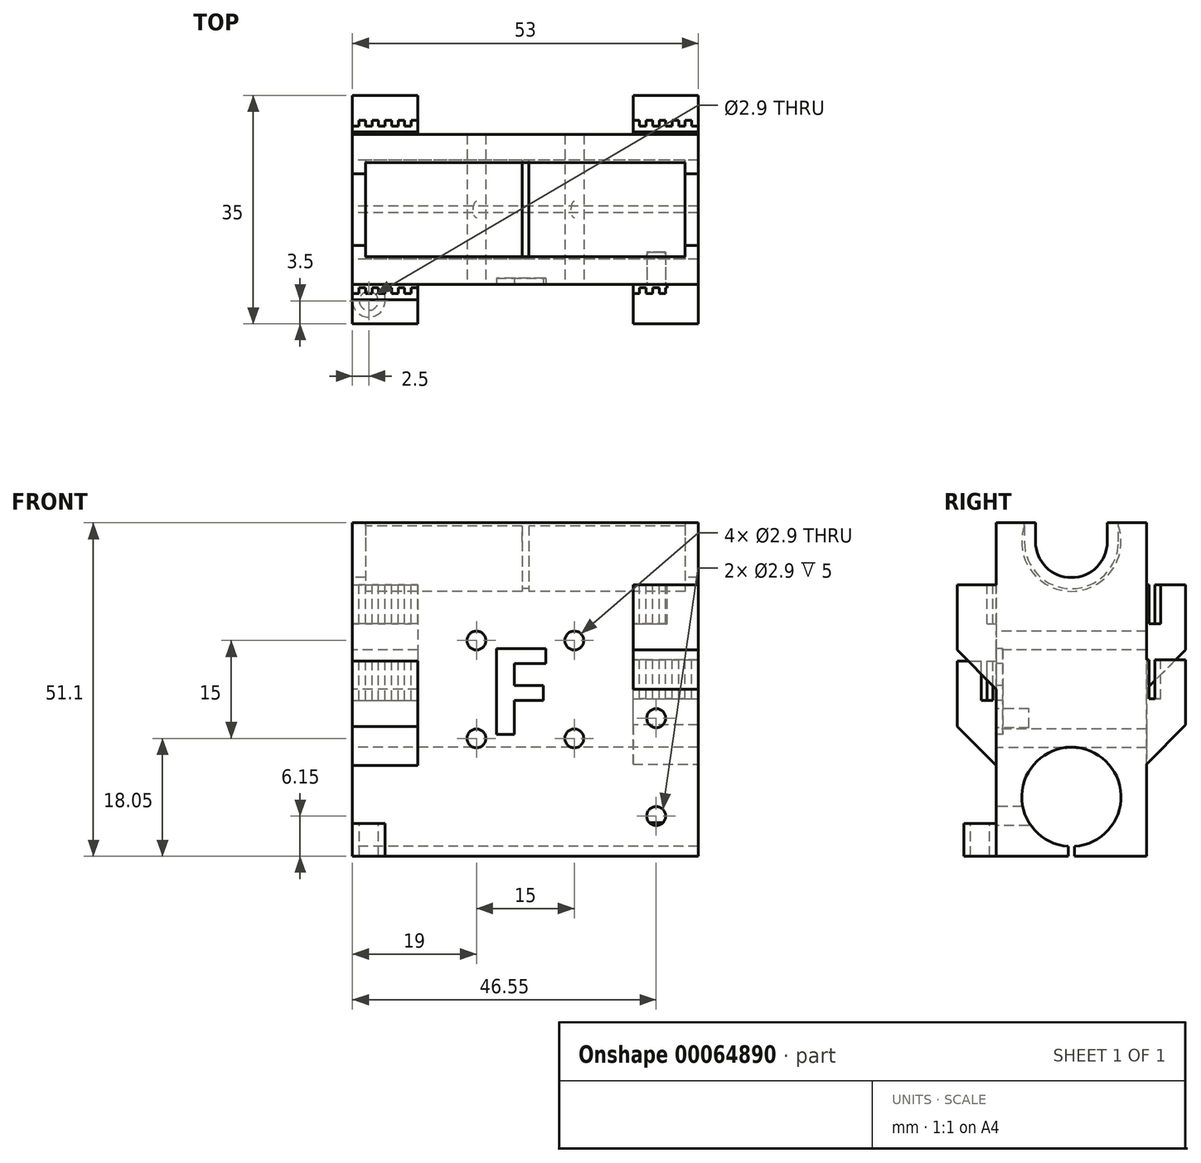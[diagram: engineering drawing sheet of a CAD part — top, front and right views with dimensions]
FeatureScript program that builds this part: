
annotation { "Feature Type Name" : "Feature", "Feature Type Description" : "" }
export const myFeature = defineFeature(function(context is Context, id is Id, definition is map)
    precondition{}
    {
        {
            assignVariable(context, id + "F0", {"name" : "LM_L", "anyValue" : 24});
        }
        {
            assignVariable(context, id + "F1", {"name" : "LM_D", "anyValue" : 15});
        }
        {
            assignVariable(context, id + "F2", {"name" : "InterAxe", "anyValue" : 39.1});
        }
        {
            var Q0;
            Q0=qCreatedBy(makeId("Top.planeOp"),FACE);
            var sketch = newSketch(context, id + "F3", { "sketchPlane" : qUnion([Q0])});
            skLineSegment(sketch, "E0.bottom", {"start": v(0, 0) * mm, "end": v(53, 0) * mm});
            skLineSegment(sketch, "E0.top", {"start": v(0, 23) * mm, "end": v(53, 23) * mm});
            skLineSegment(sketch, "E0.left", {"start": v(0, 0) * mm, "end": v(0, 23) * mm});
            skLineSegment(sketch, "E0.right", {"start": v(53, 0) * mm, "end": v(53, 23) * mm});
            skSolve(sketch);
        }
        {
            var Q0;
            Q0=qSketchRegion(id+"F3",true);
            extrude(context, id + "F4", {"entities" : qUnion([Q0]), "depth" : (getVariable(context, 'InterAxe') + getVariable(context, 'LM_D') + 1.5 - getVariable(context, 'LM_D') / 2 * 0.6) * mm});
        }
        {
            var Q0;
            Q0=makeQuery(id+"F4.opExtrude","SWEPT_FACE",FACE,{"disambiguationData":[OSD([sQuery(id+"F3.wireOp",EDGE,"E0.left")])]});
            var sketch = newSketch(context, id + "F5", { "sketchPlane" : qUnion([Q0])});
            skCircle(sketch, "E1", {"center": v(-11.5, 9.1) * mm, "radius": 7.6 * mm});
            skCircle(sketch, "E2", {"center": v(-11.5, 48.2) * mm, "radius": 5.5 * mm});
            skLineSegment(sketch, "E3", {"start": v(-23, 48.2) * mm, "end": v(0, 48.2) * mm, "construction": true});
            skLineSegment(sketch, "E4", {"start": v(-17, 51.1) * mm, "end": v(-17, 48.2) * mm});
            skLineSegment(sketch, "E5", {"start": v(-6, 51.1) * mm, "end": v(-6, 48.2) * mm});
            skLineSegment(sketch, "E6", {"start": v(-23, 9.1) * mm, "end": v(0, 9.1) * mm, "construction": true});
            skLineSegment(sketch, "E7", {"start": v(-11.5, 9.1) * mm, "end": v(-11.5, 0) * mm, "construction": true});
            skLineSegment(sketch, "E8", {"start": v(-11.5, 0) * mm, "end": v(-12, 0) * mm});
            skLineSegment(sketch, "E9", {"start": v(-12, 0) * mm, "end": v(-12, 1.52) * mm});
            skLineSegment(sketch, "E10", {"start": v(-12, 1.52) * mm, "end": v(-11, 1.52) * mm});
            skLineSegment(sketch, "E11", {"start": v(-11, 1.52) * mm, "end": v(-11, 0) * mm});
            skLineSegment(sketch, "E12", {"start": v(-11, 0) * mm, "end": v(-11.5, 0) * mm});
            skLineSegment(sketch, "E13", {"start": v(-11.5, 15.6) * mm, "end": v(-11.5, 16.7) * mm});
            skLineSegment(sketch, "E14", {"start": v(-11.5, 15.6) * mm, "end": v(-7, 15.22) * mm});
            skLineSegment(sketch, "E15", {"start": v(-11.5, 15.6) * mm, "end": v(-16, 15.22) * mm});
            skCircle(sketch, "E16", {"center": v(-11.5, 48.2) * mm, "radius": 7.6 * mm});
            skLineSegment(sketch, "E17", {"start": v(-3.9, 48.2) * mm, "end": v(-3.9, 51.1) * mm});
            skLineSegment(sketch, "E18", {"start": v(-19.1, 48.2) * mm, "end": v(-19.1, 51.1) * mm});
            skLineSegment(sketch, "E19", {"start": v(-3.9, 51.1) * mm, "end": v(-4.3, 51.1) * mm});
            skLineSegment(sketch, "E20", {"start": v(-4.3, 51.1) * mm, "end": v(-4.3, 50.63) * mm});
            skLineSegment(sketch, "E21", {"start": v(-19.1, 51.1) * mm, "end": v(-18.7, 51.1) * mm});
            skLineSegment(sketch, "E22", {"start": v(-18.7, 51.1) * mm, "end": v(-18.7, 50.63) * mm});
            skCircle(sketch, "E23", {"center": v(-11.5, 48.2) * mm, "radius": 7.2 * mm});
            skLineSegment(sketch, "E24", {"start": v(-18.7, 50.63) * mm, "end": v(-18.7, 48.2) * mm});
            skLineSegment(sketch, "E25", {"start": v(-4.3, 50.63) * mm, "end": v(-4.3, 48.2) * mm});
            skSolve(sketch);
        }
        {
            var Q0;
            {var subQ0=sQuery(id+"F5.wireOp",EDGE,"E14");var subQ1=sQuery(id+"F5.wireOp",EDGE,"E1");var subQ3=makeQuery(id+"F5.imprint","INTERSECT",VERTEX,{"disambiguationData":[OD(0.0)],"derivedFrom":[subQ1,subQ0]});Q0=makeQuery(id+"F5.imprint","IMPRINT",FACE,{"disambiguationData":[TD([[makeQuery(id+"F5.imprint","IMPRINT",EDGE,{"disambiguationData":[TD([[subQ3,-1.0]])],"derivedFrom":subQ1}),1.0]])]});}
            var Q1;
            {var subQ0=sQuery(id+"F5.wireOp",EDGE,"E15");var subQ1=sQuery(id+"F5.wireOp",EDGE,"E1");var subQ3=makeQuery(id+"F5.imprint","INTERSECT",VERTEX,{"disambiguationData":[OD(0.0)],"derivedFrom":[subQ1,subQ0]});Q1=makeQuery(id+"F5.imprint","IMPRINT",FACE,{"disambiguationData":[TD([[makeQuery(id+"F5.imprint","IMPRINT",EDGE,{"disambiguationData":[TD([[subQ3,1.0]])],"derivedFrom":subQ1}),1.0]])]});}
            var Q2;
            Q2=makeQuery(id+"F5.imprint","IMPRINT",FACE,{"disambiguationData":[TD([[makeQuery(id+"F5.imprint","IMPRINT",EDGE,{"derivedFrom":sQuery(id+"F5.wireOp",EDGE,"E8")}),-1.0]])]});
            var Q3;
            {var subQ0=sQuery(id+"F5.wireOp",EDGE,"E10");Q3=makeQuery(id+"F5.imprint","IMPRINT",FACE,{"disambiguationData":[TD([[makeQuery(id+"F5.imprint","IMPRINT",EDGE,{"derivedFrom":subQ0}),-1.0]])]});}
            var Q4;
            {var subQ3=sQuery(id+"F5.wireOp",EDGE,"E13");Q4=makeQuery(id+"F5.imprint","IMPRINT",FACE,{"disambiguationData":[TD([[makeQuery(id+"F5.imprint","IMPRINT",EDGE,{"derivedFrom":subQ3}),-1.0]])]});}
            var Q5;
            {var subQ3=sQuery(id+"F5.wireOp",EDGE,"E13");Q5=makeQuery(id+"F5.imprint","IMPRINT",FACE,{"disambiguationData":[TD([[makeQuery(id+"F5.imprint","IMPRINT",EDGE,{"derivedFrom":subQ3}),1.0]])]});}
            var Q6;
            {var subQ7=sQuery(id+"F5.wireOp",EDGE,"E10");Q6=makeQuery(id+"F5.imprint","IMPRINT",FACE,{"disambiguationData":[TD([[makeQuery(id+"F5.imprint","IMPRINT",EDGE,{"derivedFrom":subQ7}),1.0]])]});}
            var Q7;
            {var subQ3=sQuery(id+"F5.wireOp",EDGE,"E5");Q7=makeQuery(id+"F5.imprint","IMPRINT",FACE,{"disambiguationData":[TD([[makeQuery(id+"F5.imprint","IMPRINT",EDGE,{"derivedFrom":subQ3}),-1.0]])]});}
            var Q8;
            {var subQ0=sQuery(id+"F5.wireOp",EDGE,"E4");Q8=makeQuery(id+"F5.imprint","IMPRINT",FACE,{"disambiguationData":[TD([[makeQuery(id+"F5.imprint","IMPRINT",EDGE,{"derivedFrom":subQ0}),1.0]])]});}
            var Q9;
            {var subQ0=sQuery(id+"F5.wireOp",EDGE,"E4");Q9=makeQuery(id+"F5.imprint","IMPRINT",FACE,{"disambiguationData":[TD([[makeQuery(id+"F5.imprint","IMPRINT",EDGE,{"derivedFrom":subQ0}),1.0]])]});}
            var Q10;
            {var subQ3=sQuery(id+"F5.wireOp",EDGE,"E5");Q10=makeQuery(id+"F5.imprint","IMPRINT",FACE,{"disambiguationData":[TD([[makeQuery(id+"F5.imprint","IMPRINT",EDGE,{"derivedFrom":subQ3}),-1.0]])]});}
            var Q11;
            {var subQ1=sQuery(id+"F5.wireOp",EDGE,"E2");var subQ4=makeQuery(id+"F5.imprint","INTERSECT",VERTEX,{"derivedFrom":[subQ1,sQuery(id+"F5.wireOp",EDGE,"E5")]});Q11=makeQuery(id+"F5.imprint","IMPRINT",FACE,{"disambiguationData":[TD([[makeQuery(id+"F5.imprint","IMPRINT",EDGE,{"disambiguationData":[TD([[subQ4,-1.0]])],"derivedFrom":subQ1}),1.0]])]});}
            extrude(context, id + "F6", {"entities" : qUnion([Q0, Q1, Q2, Q3, Q4, Q5, Q6, Q7, Q8, Q9, Q10, Q11]), "operationType" : NewBodyOperationType.REMOVE, "endBound" : BoundingType.THROUGH_ALL, "oppositeDirection" : true, "depth" : 25 * mm});
        }
        {
            var Q0;
            {var subQ3=sQuery(id+"F5.wireOp",EDGE,"E4");Q0=makeQuery(id+"F5.imprint","IMPRINT",FACE,{"disambiguationData":[TD([[makeQuery(id+"F5.imprint","IMPRINT",EDGE,{"derivedFrom":subQ3}),-1.0]])]});}
            var Q1;
            {var subQ9=sQuery(id+"F5.wireOp",EDGE,"Eceb68xk-Og1x-mNxy-NVvu-haE7G9XDnVFp");Q1=makeQuery(id+"F5.imprint","IMPRINT",FACE,{"disambiguationData":[TD([[makeQuery(id+"F5.imprint","IMPRINT",EDGE,{"derivedFrom":subQ9}),-1.0]])]});}
            var Q2;
            {var subQ2=sQuery(id+"F5.wireOp",EDGE,"0G9KEAjU-obAv-1t8S-ChZ4-jWTQQU7pxxCP");Q2=makeQuery(id+"F5.imprint","IMPRINT",FACE,{"disambiguationData":[TD([[makeQuery(id+"F5.imprint","IMPRINT",EDGE,{"derivedFrom":subQ2}),-1.0]])]});}
            var Q3;
            {var subQ2=sQuery(id+"F5.wireOp",EDGE,"Eceb68xk-Og1x-mNxy-NVvu-haE7G9XDnVFp");Q3=makeQuery(id+"F5.imprint","IMPRINT",FACE,{"disambiguationData":[TD([[makeQuery(id+"F5.imprint","IMPRINT",EDGE,{"derivedFrom":subQ2}),1.0]])]});}
            var Q4;
            {var subQ0=sQuery(id+"F5.wireOp",EDGE,"E25");Q4=makeQuery(id+"F5.imprint","IMPRINT",FACE,{"disambiguationData":[TD([[makeQuery(id+"F5.imprint","IMPRINT",EDGE,{"derivedFrom":subQ0}),-1.0]])]});}
            var Q5;
            {var subQ0=sQuery(id+"F5.wireOp",EDGE,"E24");Q5=makeQuery(id+"F5.imprint","IMPRINT",FACE,{"disambiguationData":[TD([[makeQuery(id+"F5.imprint","IMPRINT",EDGE,{"derivedFrom":subQ0}),1.0]])]});}
            var Q6;
            {var subQ0=sQuery(id+"F5.wireOp",EDGE,"E22");Q6=makeQuery(id+"F5.imprint","IMPRINT",FACE,{"disambiguationData":[TD([[makeQuery(id+"F5.imprint","IMPRINT",EDGE,{"derivedFrom":subQ0}),1.0]])]});}
            var Q7;
            {var subQ0=sQuery(id+"F5.wireOp",EDGE,"E24");Q7=makeQuery(id+"F5.imprint","IMPRINT",FACE,{"disambiguationData":[TD([[makeQuery(id+"F5.imprint","IMPRINT",EDGE,{"derivedFrom":subQ0}),-1.0]])]});}
            var Q8;
            {var subQ0=sQuery(id+"F5.wireOp",EDGE,"E20");Q8=makeQuery(id+"F5.imprint","IMPRINT",FACE,{"disambiguationData":[TD([[makeQuery(id+"F5.imprint","IMPRINT",EDGE,{"derivedFrom":subQ0}),-1.0]])]});}
            extrude(context, id + "F7", {"entities" : qUnion([Q0, Q1, Q2, Q3, Q4, Q5, Q6, Q7, Q8]), "operationType" : NewBodyOperationType.REMOVE, "oppositeDirection" : true, "depth" : (3 + getVariable(context, 'LM_L') * 2) * mm});
        }
        {
            var Q0;
            {var subQ0=sQuery(id+"F5.wireOp",EDGE,"E24");Q0=makeQuery(id+"F5.imprint","IMPRINT",FACE,{"disambiguationData":[TD([[makeQuery(id+"F5.imprint","IMPRINT",EDGE,{"derivedFrom":subQ0}),-1.0]])]});}
            extrude(context, id + "F8", {"entities" : qUnion([Q0]), "operationType" : NewBodyOperationType.ADD, "oppositeDirection" : true, "depth" : (3 + getVariable(context, 'LM_L')) * mm});
        }
        {
            var Q0;
            {var subQ3=sQuery(id+"F5.wireOp",EDGE,"E4");Q0=makeQuery(id+"F5.imprint","IMPRINT",FACE,{"disambiguationData":[TD([[makeQuery(id+"F5.imprint","IMPRINT",EDGE,{"derivedFrom":subQ3}),-1.0]])]});}
            var Q1;
            {var subQ0=sQuery(id+"F5.wireOp",EDGE,"E20");Q1=makeQuery(id+"F5.imprint","IMPRINT",FACE,{"disambiguationData":[TD([[makeQuery(id+"F5.imprint","IMPRINT",EDGE,{"derivedFrom":subQ0}),-1.0]])]});}
            var Q2;
            {var subQ0=sQuery(id+"F5.wireOp",EDGE,"E22");Q2=makeQuery(id+"F5.imprint","IMPRINT",FACE,{"disambiguationData":[TD([[makeQuery(id+"F5.imprint","IMPRINT",EDGE,{"derivedFrom":subQ0}),1.0]])]});}
            var Q3;
            {var subQ0=sQuery(id+"F5.wireOp",EDGE,"E24");Q3=makeQuery(id+"F5.imprint","IMPRINT",FACE,{"disambiguationData":[TD([[makeQuery(id+"F5.imprint","IMPRINT",EDGE,{"derivedFrom":subQ0}),-1.0]])]});}
            var Q4;
            {var subQ0=sQuery(id+"F5.wireOp",EDGE,"E24");Q4=makeQuery(id+"F5.imprint","IMPRINT",FACE,{"disambiguationData":[TD([[makeQuery(id+"F5.imprint","IMPRINT",EDGE,{"derivedFrom":subQ0}),1.0]])]});}
            var Q5;
            {var subQ0=sQuery(id+"F5.wireOp",EDGE,"E4");Q5=makeQuery(id+"F5.imprint","IMPRINT",FACE,{"disambiguationData":[TD([[makeQuery(id+"F5.imprint","IMPRINT",EDGE,{"derivedFrom":subQ0}),1.0]])]});}
            var Q6;
            {var subQ0=sQuery(id+"F5.wireOp",EDGE,"E25");Q6=makeQuery(id+"F5.imprint","IMPRINT",FACE,{"disambiguationData":[TD([[makeQuery(id+"F5.imprint","IMPRINT",EDGE,{"derivedFrom":subQ0}),-1.0]])]});}
            extrude(context, id + "F9", {"entities" : qUnion([Q0, Q1, Q2, Q3, Q4, Q5, Q6]), "operationType" : NewBodyOperationType.REMOVE, "oppositeDirection" : true, "depth" : (2 + getVariable(context, 'LM_L')) * mm});
        }
        {
            var Q0;
            {var subQ3=sQuery(id+"F5.wireOp",EDGE,"E4");Q0=makeQuery(id+"F5.imprint","IMPRINT",FACE,{"disambiguationData":[TD([[makeQuery(id+"F5.imprint","IMPRINT",EDGE,{"derivedFrom":subQ3}),-1.0]])]});}
            var Q1;
            {var subQ3=sQuery(id+"F5.wireOp",EDGE,"E18");Q1=makeQuery(id+"F5.imprint","IMPRINT",FACE,{"disambiguationData":[TD([[makeQuery(id+"F5.imprint","IMPRINT",EDGE,{"derivedFrom":subQ3}),-1.0]])]});}
            var Q2;
            {var subQ3=sQuery(id+"F5.wireOp",EDGE,"E17");Q2=makeQuery(id+"F5.imprint","IMPRINT",FACE,{"disambiguationData":[TD([[makeQuery(id+"F5.imprint","IMPRINT",EDGE,{"derivedFrom":subQ3}),1.0]])]});}
            var Q3;
            {var subQ0=sQuery(id+"F5.wireOp",EDGE,"E24");Q3=makeQuery(id+"F5.imprint","IMPRINT",FACE,{"disambiguationData":[TD([[makeQuery(id+"F5.imprint","IMPRINT",EDGE,{"derivedFrom":subQ0}),-1.0]])]});}
            var Q4;
            {var subQ0=sQuery(id+"F5.wireOp",EDGE,"E24");Q4=makeQuery(id+"F5.imprint","IMPRINT",FACE,{"disambiguationData":[TD([[makeQuery(id+"F5.imprint","IMPRINT",EDGE,{"derivedFrom":subQ0}),1.0]])]});}
            var Q5;
            {var subQ0=sQuery(id+"F5.wireOp",EDGE,"E22");Q5=makeQuery(id+"F5.imprint","IMPRINT",FACE,{"disambiguationData":[TD([[makeQuery(id+"F5.imprint","IMPRINT",EDGE,{"derivedFrom":subQ0}),1.0]])]});}
            var Q6;
            {var subQ0=sQuery(id+"F5.wireOp",EDGE,"E25");Q6=makeQuery(id+"F5.imprint","IMPRINT",FACE,{"disambiguationData":[TD([[makeQuery(id+"F5.imprint","IMPRINT",EDGE,{"derivedFrom":subQ0}),-1.0]])]});}
            var Q7;
            {var subQ0=sQuery(id+"F5.wireOp",EDGE,"E20");Q7=makeQuery(id+"F5.imprint","IMPRINT",FACE,{"disambiguationData":[TD([[makeQuery(id+"F5.imprint","IMPRINT",EDGE,{"derivedFrom":subQ0}),-1.0]])]});}
            extrude(context, id + "F10", {"entities" : qUnion([Q0, Q1, Q2, Q3, Q4, Q5, Q6, Q7]), "operationType" : NewBodyOperationType.ADD, "oppositeDirection" : true, "depth" : 2 * mm});
        }
        {
            var Q0;
            Q0=makeQuery(id+"F4.opExtrude","SWEPT_FACE",FACE,{"disambiguationData":[OSD([sQuery(id+"F3.wireOp",EDGE,"E0.bottom")])]});
            var sketch = newSketch(context, id + "F11", { "sketchPlane" : qUnion([Q0])});
            skLineSegment(sketch, "E26.bottom", {"start": v(0, 29.9) * mm, "end": v(10, 29.9) * mm});
            skLineSegment(sketch, "E26.top", {"start": v(0, 9.9) * mm, "end": v(10, 9.9) * mm});
            skLineSegment(sketch, "E26.left", {"start": v(0, 29.9) * mm, "end": v(0, 9.9) * mm});
            skLineSegment(sketch, "E26.right", {"start": v(10, 29.9) * mm, "end": v(10, 9.9) * mm});
            skLineSegment(sketch, "E27.bottom", {"start": v(53, 41.6) * mm, "end": v(43, 41.6) * mm});
            skLineSegment(sketch, "E27.top", {"start": v(53, 21.6) * mm, "end": v(43, 21.6) * mm});
            skLineSegment(sketch, "E27.left", {"start": v(53, 41.6) * mm, "end": v(53, 21.6) * mm});
            skLineSegment(sketch, "E27.right", {"start": v(43, 41.6) * mm, "end": v(43, 21.6) * mm});
            skPoint(sketch, "E28", {"position": v(0, 48.1) * mm});
            skPoint(sketch, "E29", {"position": v(0, 9.4) * mm});
            skSolve(sketch);
        }
        {
            var Q0;
            Q0=qSketchRegion(id+"F11",true);
            extrude(context, id + "F12", {"entities" : qUnion([Q0]), "operationType" : NewBodyOperationType.ADD, "depth" : 6 * mm});
        }
        {
            var Q0;
            Q0=makeQuery(id+"F12.opExtrude","CAP_EDGE",EDGE,{"disambiguationData":[OSD([sQuery(id+"F11.wireOp",EDGE,"E26.top")])],"isStart":false});
            var Q1;
            Q1=makeQuery(id+"F12.opExtrude","CAP_EDGE",EDGE,{"disambiguationData":[OSD([sQuery(id+"F11.wireOp",EDGE,"E27.top")])],"isStart":false});
            chamfer(context, id + "F13", {"entities" : qUnion([Q0, Q1]), "width" : 10 * mm, "tangentPropagation" : true});
        }
        {
            var Q0;
            Q0=makeQuery(id+"F12.opExtrude","SWEPT_FACE",FACE,{"disambiguationData":[OSD([sQuery(id+"F11.wireOp",EDGE,"E26.bottom")])]});
            var sketch = newSketch(context, id + "F14", { "sketchPlane" : qUnion([Q0])});
            skLineSegment(sketch, "E30.left", {"start": v(0, -2.3) * mm, "end": v(0, -0.5) * mm});
            skLineSegment(sketch, "E31", {"start": v(6, -1.4) * mm, "end": v(7, -1.4) * mm});
            skLineSegment(sketch, "E32", {"start": v(4, -1.4) * mm, "end": v(5, -1.4) * mm});
            skLineSegment(sketch, "E33", {"start": v(0, -1.4) * mm, "end": v(1, -1.4) * mm});
            skLineSegment(sketch, "E34", {"start": v(7, -0.5) * mm, "end": v(8, -0.5) * mm});
            skLineSegment(sketch, "E35", {"start": v(2, -1.4) * mm, "end": v(3, -1.4) * mm});
            skLineSegment(sketch, "E36", {"start": v(3, -0.5) * mm, "end": v(4, -0.5) * mm});
            skLineSegment(sketch, "E37", {"start": v(8, -1.4) * mm, "end": v(9, -1.4) * mm});
            skLineSegment(sketch, "E38", {"start": v(8, -0.5) * mm, "end": v(8, -1.4) * mm});
            skLineSegment(sketch, "E39", {"start": v(9, -1.4) * mm, "end": v(9, -0.5) * mm});
            skLineSegment(sketch, "E40", {"start": v(10, -0.5) * mm, "end": v(10, -1.4) * mm});
            skLineSegment(sketch, "E41", {"start": v(6, -0.5) * mm, "end": v(6, -1.4) * mm});
            skLineSegment(sketch, "E42", {"start": v(2, -0.5) * mm, "end": v(2, -1.4) * mm});
            skLineSegment(sketch, "E43", {"start": v(1, -0.5) * mm, "end": v(2, -0.5) * mm});
            skLineSegment(sketch, "E44", {"start": v(1, -1.4) * mm, "end": v(1, -0.5) * mm});
            skLineSegment(sketch, "E45", {"start": v(9, -0.5) * mm, "end": v(10, -0.5) * mm});
            skLineSegment(sketch, "E46", {"start": v(5, -0.5) * mm, "end": v(6, -0.5) * mm});
            skLineSegment(sketch, "E47", {"start": v(5, -1.4) * mm, "end": v(5, -0.5) * mm});
            skLineSegment(sketch, "E48", {"start": v(3, -1.4) * mm, "end": v(3, -0.5) * mm});
            skLineSegment(sketch, "E49", {"start": v(4, -0.5) * mm, "end": v(4, -1.4) * mm});
            skLineSegment(sketch, "E50", {"start": v(7, -1.4) * mm, "end": v(7, -0.5) * mm});
            skLineSegment(sketch, "E51", {"start": v(0, -0.5) * mm, "end": v(0, -1.4) * mm});
            skLineSegment(sketch, "E52", {"start": v(10, -1.4) * mm, "end": v(10, -2.3) * mm});
            skLineSegment(sketch, "E53", {"start": v(0, -2.3) * mm, "end": v(10, -2.3) * mm});
            skLineSegment(sketch, "E54", {"start": v(5.3, -0.5) * mm, "end": v(5.3, 0) * mm});
            skSolve(sketch);
        }
        {
            var Q0;
            Q0=qSketchRegion(id+"F14",true);
            extrude(context, id + "F15", {"entities" : qUnion([Q0]), "operationType" : NewBodyOperationType.REMOVE, "oppositeDirection" : true, "depth" : 6 * mm});
        }
        {
            var Q0;
            Q0=makeQuery(id+"F12.opExtrude","SWEPT_FACE",FACE,{"disambiguationData":[OSD([sQuery(id+"F11.wireOp",EDGE,"E27.bottom")])]});
            var sketch = newSketch(context, id + "F16", { "sketchPlane" : qUnion([Q0])});
            skLineSegment(sketch, "E55.left", {"start": v(43, -2.3) * mm, "end": v(43, -0.5) * mm});
            skLineSegment(sketch, "E56", {"start": v(49, -1.4) * mm, "end": v(50, -1.4) * mm});
            skLineSegment(sketch, "E57", {"start": v(47, -1.4) * mm, "end": v(48, -1.4) * mm});
            skLineSegment(sketch, "E58", {"start": v(43, -1.4) * mm, "end": v(44, -1.4) * mm});
            skLineSegment(sketch, "E59", {"start": v(50, -0.5) * mm, "end": v(51, -0.5) * mm});
            skLineSegment(sketch, "E60", {"start": v(45, -1.4) * mm, "end": v(46, -1.4) * mm});
            skLineSegment(sketch, "E61", {"start": v(46, -0.5) * mm, "end": v(47, -0.5) * mm});
            skLineSegment(sketch, "E62", {"start": v(51, -1.4) * mm, "end": v(52, -1.4) * mm});
            skLineSegment(sketch, "E63", {"start": v(51, -0.5) * mm, "end": v(51, -1.4) * mm});
            skLineSegment(sketch, "E64", {"start": v(52, -1.4) * mm, "end": v(52, -0.5) * mm});
            skLineSegment(sketch, "E65", {"start": v(53, -0.5) * mm, "end": v(53, -1.4) * mm});
            skLineSegment(sketch, "E66", {"start": v(49, -0.5) * mm, "end": v(49, -1.4) * mm});
            skLineSegment(sketch, "E67", {"start": v(45, -0.5) * mm, "end": v(45, -1.4) * mm});
            skLineSegment(sketch, "E68", {"start": v(44, -0.5) * mm, "end": v(45, -0.5) * mm});
            skLineSegment(sketch, "E69", {"start": v(44, -1.4) * mm, "end": v(44, -0.5) * mm});
            skLineSegment(sketch, "E70", {"start": v(52, -0.5) * mm, "end": v(53, -0.5) * mm});
            skLineSegment(sketch, "E71", {"start": v(48, -0.5) * mm, "end": v(49, -0.5) * mm});
            skLineSegment(sketch, "E72", {"start": v(48, -1.4) * mm, "end": v(48, -0.5) * mm});
            skLineSegment(sketch, "E73", {"start": v(46, -1.4) * mm, "end": v(46, -0.5) * mm});
            skLineSegment(sketch, "E74", {"start": v(47, -0.5) * mm, "end": v(47, -1.4) * mm});
            skLineSegment(sketch, "E75", {"start": v(50, -1.4) * mm, "end": v(50, -0.5) * mm});
            skLineSegment(sketch, "E76", {"start": v(43, -0.5) * mm, "end": v(43, -1.4) * mm});
            skLineSegment(sketch, "E77", {"start": v(53, -1.4) * mm, "end": v(53, -2.3) * mm});
            skLineSegment(sketch, "E78", {"start": v(43, -2.3) * mm, "end": v(53, -2.3) * mm});
            skLineSegment(sketch, "E79", {"start": v(48.23, -0.5) * mm, "end": v(48.23, 0) * mm});
            skSolve(sketch);
        }
        {
            var Q0;
            Q0=makeQuery(id+"F4.opExtrude","SWEPT_FACE",FACE,{"disambiguationData":[OSD([sQuery(id+"F3.wireOp",EDGE,"E0.top")])]});
            var sketch = newSketch(context, id + "F17", { "sketchPlane" : qUnion([Q0])});
            skLineSegment(sketch, "E80.bottom", {"start": v(-53, 10.1) * mm, "end": v(-43, 10.1) * mm});
            skLineSegment(sketch, "E80.top", {"start": v(-53, 30.1) * mm, "end": v(-43, 30.1) * mm});
            skLineSegment(sketch, "E80.left", {"start": v(-53, 10.1) * mm, "end": v(-53, 30.1) * mm});
            skLineSegment(sketch, "E80.right", {"start": v(-43, 10.1) * mm, "end": v(-43, 30.1) * mm});
            skLineSegment(sketch, "E81.bottom", {"start": v(0, 41.6) * mm, "end": v(-10, 41.6) * mm});
            skLineSegment(sketch, "E81.top", {"start": v(0, 21.6) * mm, "end": v(-10, 21.6) * mm});
            skLineSegment(sketch, "E81.left", {"start": v(0, 41.6) * mm, "end": v(0, 21.6) * mm});
            skLineSegment(sketch, "E81.right", {"start": v(-10, 41.6) * mm, "end": v(-10, 21.6) * mm});
            skSolve(sketch);
        }
        {
            var Q0;
            Q0=qSketchRegion(id+"F17",true);
            extrude(context, id + "F18", {"entities" : qUnion([Q0]), "operationType" : NewBodyOperationType.ADD, "depth" : 6 * mm});
        }
        {
            var Q0;
            Q0=makeQuery(id+"F18.opExtrude","SWEPT_FACE",FACE,{"disambiguationData":[OSD([sQuery(id+"F17.wireOp",EDGE,"E80.top")])]});
            var sketch = newSketch(context, id + "F19", { "sketchPlane" : qUnion([Q0])});
            skLineSegment(sketch, "E82", {"start": v(45, 23.4) * mm, "end": v(46, 23.4) * mm});
            skLineSegment(sketch, "E83", {"start": v(46, 24.3) * mm, "end": v(47, 24.3) * mm});
            skLineSegment(sketch, "E84", {"start": v(52, 24.3) * mm, "end": v(53, 24.3) * mm});
            skLineSegment(sketch, "E85", {"start": v(53, 23.4) * mm, "end": v(53, 23.4) * mm});
            skLineSegment(sketch, "E86", {"start": v(43, 23.4) * mm, "end": v(53, 23.4) * mm});
            skLineSegment(sketch, "E87", {"start": v(48, 23.4) * mm, "end": v(48, 23) * mm});
            skLineSegment(sketch, "E88", {"start": v(43, 25.2) * mm, "end": v(53, 25.2) * mm});
            skLineSegment(sketch, "E89.bottom", {"start": v(47, 24.3) * mm, "end": v(46, 24.3) * mm});
            skLineSegment(sketch, "E89.top", {"start": v(47, 25.2) * mm, "end": v(46, 25.2) * mm});
            skLineSegment(sketch, "E90.top", {"start": v(48, 25.2) * mm, "end": v(49, 25.2) * mm});
            skLineSegment(sketch, "E91.top", {"start": v(44, 25.2) * mm, "end": v(45, 25.2) * mm});
            skLineSegment(sketch, "E92", {"start": v(53, 24.3) * mm, "end": v(43, 24.3) * mm, "construction": true});
            skLineSegment(sketch, "E93", {"start": v(52, 24.3) * mm, "end": v(52, 25.2) * mm});
            skLineSegment(sketch, "E94.1.0.0", {"start": v(51, 24.3) * mm, "end": v(51, 25.2) * mm});
            skLineSegment(sketch, "E94.2.0.0", {"start": v(50, 24.3) * mm, "end": v(50, 25.2) * mm});
            skLineSegment(sketch, "E94.3.0.0", {"start": v(49, 24.3) * mm, "end": v(49, 25.2) * mm});
            skLineSegment(sketch, "E94.4.0.0", {"start": v(48, 24.3) * mm, "end": v(48, 25.2) * mm});
            skLineSegment(sketch, "E94.5.0.0", {"start": v(47, 24.3) * mm, "end": v(47, 25.2) * mm});
            skLineSegment(sketch, "E94.6.0.0", {"start": v(46, 24.3) * mm, "end": v(46, 25.2) * mm});
            skLineSegment(sketch, "E94.7.0.0", {"start": v(45, 24.3) * mm, "end": v(45, 25.2) * mm});
            skLineSegment(sketch, "E94.8.0.0", {"start": v(44, 24.3) * mm, "end": v(44, 25.2) * mm});
            skLineSegment(sketch, "E94.direction1", {"start": v(52, 24.3) * mm, "end": v(51, 24.3) * mm, "construction": true});
            skLineSegment(sketch, "E95", {"start": v(51, 24.3) * mm, "end": v(50, 24.3) * mm});
            skLineSegment(sketch, "E96", {"start": v(49, 24.3) * mm, "end": v(48, 24.3) * mm});
            skLineSegment(sketch, "E97", {"start": v(45, 24.3) * mm, "end": v(44, 24.3) * mm});
            skSolve(sketch);
        }
        {
            var Q0;
            {var subQ10=sQuery(id+"F19.wireOp",EDGE,"E84");Q0=makeQuery(id+"F19.imprint","IMPRINT",FACE,{"disambiguationData":[TD([[makeQuery(id+"F19.imprint","IMPRINT",EDGE,{"derivedFrom":subQ10}),-1.0]])]});}
            extrude(context, id + "F20", {"entities" : qUnion([Q0]), "operationType" : NewBodyOperationType.REMOVE, "oppositeDirection" : true, "depth" : 6 * mm});
        }
        {
            var Q0;
            Q0=makeQuery(id+"F18.opExtrude","SWEPT_FACE",FACE,{"disambiguationData":[OSD([sQuery(id+"F17.wireOp",EDGE,"E81.bottom")])]});
            var sketch = newSketch(context, id + "F21", { "sketchPlane" : qUnion([Q0])});
            skLineSegment(sketch, "E98", {"start": v(10, 25.2) * mm, "end": v(0, 25.2) * mm});
            skLineSegment(sketch, "E99", {"start": v(10, 23.4) * mm, "end": v(0, 23.4) * mm});
            skLineSegment(sketch, "E100", {"start": v(0, 23.4) * mm, "end": v(0, 24.3) * mm, "construction": true});
            skLineSegment(sketch, "E101", {"start": v(0, 25.2) * mm, "end": v(0, 24.3) * mm});
            skLineSegment(sketch, "E102", {"start": v(0, 24.3) * mm, "end": v(1, 24.3) * mm});
            skLineSegment(sketch, "E103", {"start": v(1, 24.3) * mm, "end": v(1, 25.2) * mm});
            skLineSegment(sketch, "E104.1.0.0", {"start": v(3, 24.3) * mm, "end": v(3, 25.2) * mm});
            skLineSegment(sketch, "E104.1.0.1", {"start": v(2, 24.3) * mm, "end": v(3, 24.3) * mm});
            skLineSegment(sketch, "E104.1.0.2", {"start": v(2, 25.2) * mm, "end": v(2, 24.3) * mm});
            skLineSegment(sketch, "E104.2.0.0", {"start": v(5, 24.3) * mm, "end": v(5, 25.2) * mm});
            skLineSegment(sketch, "E104.2.0.1", {"start": v(4, 24.3) * mm, "end": v(5, 24.3) * mm});
            skLineSegment(sketch, "E104.2.0.2", {"start": v(4, 25.2) * mm, "end": v(4, 24.3) * mm});
            skLineSegment(sketch, "E104.3.0.0", {"start": v(7, 24.3) * mm, "end": v(7, 25.2) * mm});
            skLineSegment(sketch, "E104.3.0.1", {"start": v(6, 24.3) * mm, "end": v(7, 24.3) * mm});
            skLineSegment(sketch, "E104.3.0.2", {"start": v(6, 25.2) * mm, "end": v(6, 24.3) * mm});
            skLineSegment(sketch, "E104.4.0.0", {"start": v(9, 24.3) * mm, "end": v(9, 25.2) * mm});
            skLineSegment(sketch, "E104.4.0.1", {"start": v(8, 24.3) * mm, "end": v(9, 24.3) * mm});
            skLineSegment(sketch, "E104.4.0.2", {"start": v(8, 25.2) * mm, "end": v(8, 24.3) * mm});
            skLineSegment(sketch, "E104.direction1", {"start": v(0, 24.3) * mm, "end": v(2, 24.3) * mm, "construction": true});
            skSolve(sketch);
        }
        {
            var Q0;
            {var subQ9=sQuery(id+"F21.wireOp",EDGE,"E99");Q0=makeQuery(id+"F21.imprint","IMPRINT",FACE,{"disambiguationData":[TD([[makeQuery(id+"F21.imprint","IMPRINT",EDGE,{"derivedFrom":subQ9}),-1.0]])]});}
            extrude(context, id + "F22", {"entities" : qUnion([Q0]), "operationType" : NewBodyOperationType.REMOVE, "oppositeDirection" : true, "depth" : 6 * mm});
        }
        {
            var Q0;
            Q0=makeQuery(id+"F18.opExtrude","CAP_EDGE",EDGE,{"disambiguationData":[OSD([sQuery(id+"F17.wireOp",EDGE,"E81.top")])],"isStart":false});
            var Q1;
            Q1=makeQuery(id+"F18.opExtrude","CAP_EDGE",EDGE,{"disambiguationData":[OSD([sQuery(id+"F17.wireOp",EDGE,"E80.bottom")])],"isStart":false});
            chamfer(context, id + "F23", {"entities" : qUnion([Q0, Q1]), "width" : 10 * mm, "tangentPropagation" : true});
        }
        {
            var Q0;
            Q0=makeQuery(id+"F4.opExtrude","SWEPT_FACE",FACE,{"disambiguationData":[OSD([sQuery(id+"F3.wireOp",EDGE,"E0.bottom")])]});
            var sketch = newSketch(context, id + "F24", { "sketchPlane" : qUnion([Q0])});
            skCircle(sketch, "E105", {"center": v(19, 33.05) * mm, "radius": 1.45 * mm});
            skCircle(sketch, "E106", {"center": v(34, 33.05) * mm, "radius": 1.45 * mm});
            skCircle(sketch, "E107", {"center": v(19, 18.05) * mm, "radius": 1.45 * mm});
            skCircle(sketch, "E108", {"center": v(34, 18.05) * mm, "radius": 1.45 * mm});
            skLineSegment(sketch, "E109", {"start": v(19, 33.05) * mm, "end": v(0, 33.05) * mm});
            skLineSegment(sketch, "E110", {"start": v(34, 18.05) * mm, "end": v(53, 18.05) * mm});
            skLineSegment(sketch, "E111", {"start": v(34, 33.05) * mm, "end": v(34, 51.1) * mm});
            skLineSegment(sketch, "E112", {"start": v(19, 18.05) * mm, "end": v(19, 0) * mm});
            skLineSegment(sketch, "E113", {"start": v(26.5, 0) * mm, "end": v(26.5, 13.82) * mm, "construction": true});
            skSolve(sketch);
        }
        {
            var Q0;
            Q0=qSketchRegion(id+"F24",true);
            var Q1;
            Q1=makeQuery(id+"F24.imprint","IMPRINT",FACE,{"disambiguationData":[TD([[makeQuery(id+"F24.imprint","IMPRINT",EDGE,{"derivedFrom":sQuery(id+"F24.wireOp",EDGE,"E105")}),1.0]])]});
            var Q2;
            Q2=makeQuery(id+"F24.imprint","IMPRINT",FACE,{"disambiguationData":[TD([[makeQuery(id+"F24.imprint","IMPRINT",EDGE,{"derivedFrom":sQuery(id+"F24.wireOp",EDGE,"E106")}),1.0]])]});
            var Q3;
            Q3=makeQuery(id+"F24.imprint","IMPRINT",FACE,{"disambiguationData":[TD([[makeQuery(id+"F24.imprint","IMPRINT",EDGE,{"derivedFrom":sQuery(id+"F24.wireOp",EDGE,"E108")}),1.0]])]});
            var Q4;
            Q4=makeQuery(id+"F24.imprint","IMPRINT",FACE,{"disambiguationData":[TD([[makeQuery(id+"F24.imprint","IMPRINT",EDGE,{"derivedFrom":sQuery(id+"F24.wireOp",EDGE,"E107")}),1.0]])]});
            extrude(context, id + "F25", {"entities" : qUnion([Q0, Q1, Q2, Q3, Q4]), "operationType" : NewBodyOperationType.REMOVE, "endBound" : BoundingType.THROUGH_ALL, "oppositeDirection" : true, "depth" : 25 * mm});
        }
        {
            var Q0;
            Q0=makeQuery(id+"F4.opExtrude","SWEPT_FACE",FACE,{"disambiguationData":[OSD([sQuery(id+"F3.wireOp",EDGE,"E0.bottom")])]});
            var sketch = newSketch(context, id + "F26", { "sketchPlane" : qUnion([Q0])});
            skCircle(sketch, "E114", {"center": v(46.55, 21.15) * mm, "radius": 1.45 * mm});
            skCircle(sketch, "E115", {"center": v(46.55, 6.15) * mm, "radius": 1.45 * mm});
            skSolve(sketch);
        }
        {
            var Q0;
            Q0=qSketchRegion(id+"F26",true);
            extrude(context, id + "F27", {"entities" : qUnion([Q0]), "operationType" : NewBodyOperationType.REMOVE, "oppositeDirection" : true, "depth" : 5 * mm});
        }
        {
            var Q0;
            Q0=makeQuery(id+"F4.opExtrude","SWEPT_FACE",FACE,{"disambiguationData":[OSD([sQuery(id+"F3.wireOp",EDGE,"E0.bottom")])]});
            var sketch = newSketch(context, id + "F28", { "sketchPlane" : qUnion([Q0])});
            skText(sketch, "E116", { "text": "F", "fontName": "OpenSans-Bold.ttf"});
            skLineSegment(sketch, "E117", {"start": v(19, 33.05) * mm, "end": v(19, 18.05) * mm, "construction": true});
            skLineSegment(sketch, "E118", {"start": v(19, 18.05) * mm, "end": v(34, 18.05) * mm, "construction": true});
            skLineSegment(sketch, "E119", {"start": v(34, 18.05) * mm, "end": v(34, 33.05) * mm, "construction": true});
            skLineSegment(sketch, "E120", {"start": v(34, 33.05) * mm, "end": v(19, 33.05) * mm, "construction": true});
            skLineSegment(sketch, "E121", {"start": v(19, 25.55) * mm, "end": v(21.9, 25.55) * mm, "construction": true});
            skLineSegment(sketch, "E122", {"start": v(31.1, 25.55) * mm, "end": v(34, 25.55) * mm, "construction": true});
            skLineSegment(sketch, "E123", {"start": v(26.5, 18.91) * mm, "end": v(26.5, 18.05) * mm, "construction": true});
            skLineSegment(sketch, "E124", {"start": v(26.5, 33.05) * mm, "end": v(26.5, 32.19) * mm, "construction": true});
            const initialGuessF28  = {"E116": [0.0204, 0.01866, 1, 0, 0.01328]};
            skSetInitialGuess(sketch, initialGuessF28);
            skSolve(sketch);
        }
        {
            var Q0;
            Q0=qSketchRegion(id+"F28",true);
            extrude(context, id + "F29", {"entities" : qUnion([Q0]), "operationType" : NewBodyOperationType.REMOVE, "oppositeDirection" : true, "depth" : 1 * mm});
        }
        {
            var Q0;
            Q0=makeQuery(id+"F4.opExtrude","SWEPT_FACE",FACE,{"disambiguationData":[OSD([sQuery(id+"F3.wireOp",EDGE,"E0.bottom")])]});
            var sketch = newSketch(context, id + "F30", { "sketchPlane" : qUnion([Q0])});
            skLineSegment(sketch, "E125.bottom", {"start": v(0, 0) * mm, "end": v(5, 0) * mm});
            skLineSegment(sketch, "E125.top", {"start": v(0, 5) * mm, "end": v(5, 5) * mm});
            skLineSegment(sketch, "E125.left", {"start": v(0, 0) * mm, "end": v(0, 5) * mm});
            skLineSegment(sketch, "E125.right", {"start": v(5, 0) * mm, "end": v(5, 5) * mm});
            skSolve(sketch);
        }
        {
            var Q0;
            Q0=qSketchRegion(id+"F30",true);
            extrude(context, id + "F31", {"entities" : qUnion([Q0]), "operationType" : NewBodyOperationType.ADD, "depth" : 5 * mm});
        }
        {
            var Q0;
            Q0=makeQuery(id+"F31.opExtrude","SWEPT_FACE",FACE,{"disambiguationData":[OSD([sQuery(id+"F30.wireOp",EDGE,"E125.top")])]});
            var sketch = newSketch(context, id + "F32", { "sketchPlane" : qUnion([Q0])});
            skCircle(sketch, "E126", {"center": v(2.5, -2.5) * mm, "radius": 1.45 * mm});
            skLineSegment(sketch, "E127", {"start": v(0, -2.5) * mm, "end": v(5, -2.5) * mm});
            skSolve(sketch);
        }
        {
            var Q0;
            Q0=qSketchRegion(id+"F32",true);
            extrude(context, id + "F33", {"entities" : qUnion([Q0]), "operationType" : NewBodyOperationType.REMOVE, "oppositeDirection" : true, "depth" : 25 * mm});
        }
        {
            var Q0;
            Q0=makeQuery(id+"F31.opExtrude","CAP_EDGE",EDGE,{"disambiguationData":[OSD([sQuery(id+"F30.wireOp",EDGE,"E125.left")])],"isStart":false});
            var Q1;
            Q1=makeQuery(id+"F31.opExtrude","CAP_EDGE",EDGE,{"disambiguationData":[OSD([sQuery(id+"F30.wireOp",EDGE,"E125.right")])],"isStart":false});
            fillet(context, id + "F34", {"entities" : qUnion([Q0, Q1]), "radius" : 2.5 * mm, "tangentPropagation" : true, "allowEdgeOverflow" : false});
        }
        {
            var Q0;
            Q0=makeQuery(id+"F16.imprint","IMPRINT",FACE,{"disambiguationData":[TD([[makeQuery(id+"F16.imprint","IMPRINT",EDGE,{"derivedFrom":sQuery(id+"F16.wireOp",EDGE,"E55.left")}),-1.0]])]});
            extrude(context, id + "F35", {"entities" : qUnion([Q0]), "operationType" : NewBodyOperationType.REMOVE, "oppositeDirection" : true, "depth" : 6 * mm});
        }
    });
